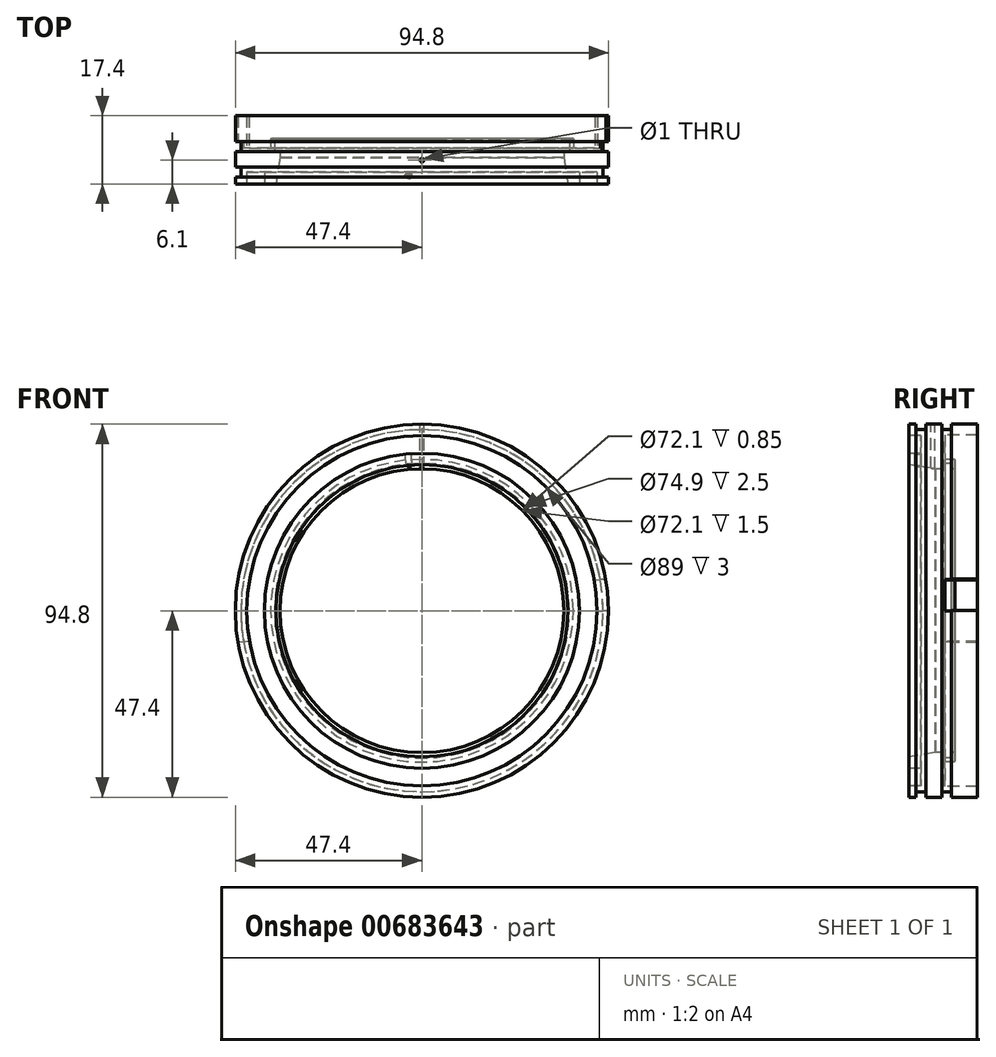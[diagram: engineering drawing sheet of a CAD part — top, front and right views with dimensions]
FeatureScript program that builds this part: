
annotation { "Feature Type Name" : "Feature", "Feature Type Description" : "" }
export const myFeature = defineFeature(function(context is Context, id is Id, definition is map)
    precondition{}
    {
        {
            var Q0;
            Q0=qCreatedBy(makeId("Right.planeOp"),FACE);
            var sketch = newSketch(context, id + "F0", { "sketchPlane" : qUnion([Q0])});
            skLineSegment(sketch, "E0", {"start": v(-21.1, 0) * mm, "end": v(20.57, 0) * mm, "construction": true});
            skLineSegment(sketch, "E1", {"start": v(0, -47.4) * mm, "end": v(1.8, -47.4) * mm});
            skLineSegment(sketch, "E2", {"start": v(1.8, -47.4) * mm, "end": v(1.8, -46) * mm});
            skLineSegment(sketch, "E3", {"start": v(1.8, -46) * mm, "end": v(4.3, -46) * mm});
            skLineSegment(sketch, "E4", {"start": v(4.3, -46) * mm, "end": v(4.3, -47.4) * mm});
            skLineSegment(sketch, "E5", {"start": v(4.3, -47.4) * mm, "end": v(8.3, -47.4) * mm});
            skLineSegment(sketch, "E6", {"start": v(8.3, -47.4) * mm, "end": v(8.3, -46) * mm});
            skLineSegment(sketch, "E7", {"start": v(8.3, -46) * mm, "end": v(10.8, -46) * mm});
            skLineSegment(sketch, "E8", {"start": v(10.8, -46) * mm, "end": v(10.8, -47.4) * mm});
            skLineSegment(sketch, "E9", {"start": v(10.8, -47.4) * mm, "end": v(17.4, -47.4) * mm});
            skLineSegment(sketch, "E10", {"start": v(17.4, -47.4) * mm, "end": v(17.4, -44.6) * mm});
            skLineSegment(sketch, "E11", {"start": v(17.4, -44.6) * mm, "end": v(9.1, -44.6) * mm});
            skLineSegment(sketch, "E12", {"start": v(9.1, -44.6) * mm, "end": v(9.1, -38.45) * mm});
            skLineSegment(sketch, "E13", {"start": v(9.1, -38.45) * mm, "end": v(11.6, -38.45) * mm});
            skLineSegment(sketch, "E14", {"start": v(11.6, -38.45) * mm, "end": v(11.6, -36.05) * mm});
            skLineSegment(sketch, "E15", {"start": v(11.6, -36.05) * mm, "end": v(10.75, -36.05) * mm});
            skLineSegment(sketch, "E16", {"start": v(10.75, -36.05) * mm, "end": v(10.75, -37.45) * mm});
            skLineSegment(sketch, "E17", {"start": v(10.75, -37.45) * mm, "end": v(8.25, -37.45) * mm});
            skLineSegment(sketch, "E18", {"start": v(8.25, -37.45) * mm, "end": v(8.25, -36.05) * mm});
            skLineSegment(sketch, "E19", {"start": v(8.25, -36.05) * mm, "end": v(6.75, -36.05) * mm});
            skLineSegment(sketch, "E20", {"start": v(6.75, -36.05) * mm, "end": v(0, -37.1) * mm});
            skLineSegment(sketch, "E21", {"start": v(0, -37.1) * mm, "end": v(0, -40) * mm});
            skLineSegment(sketch, "E22", {"start": v(0, -40) * mm, "end": v(3, -40) * mm});
            skLineSegment(sketch, "E23", {"start": v(3, -40) * mm, "end": v(3, -44.5) * mm});
            skLineSegment(sketch, "E24", {"start": v(3, -44.5) * mm, "end": v(0, -44.5) * mm});
            skLineSegment(sketch, "E25", {"start": v(0, -44.5) * mm, "end": v(0, -47.4) * mm});
            skSolve(sketch);
        }
        {
            var Q0;
            Q0=makeQuery(id+"F0.imprint","IMPRINT",FACE,{"disambiguationData":[TD([[makeQuery(id+"F0.imprint","IMPRINT",EDGE,{"derivedFrom":sQuery(id+"F0.wireOp",EDGE,"E1")}),1.0]])]});
            var Q1;
            Q1=sQuery(id+"F0.wireOp",EDGE,"E0");
            revolve(context, id + "F1", {"entities" : qUnion([Q0]), "axis" : qUnion([Q1]), "revolveType" : RevolveType.FULL});
        }
        {
            var Q0;
            Q0=qCreatedBy(makeId("Right.planeOp"),FACE);
            cPlane(context, id + "F2", {"entities" : qUnion([Q0]), "cplaneType" : CPlaneType.OFFSET, "offset" : 50 * mm, "width" : 150 * mm, "height" : 150 * mm});
        }
        {
            var Q0;
            Q0=qCreatedBy(id+"F2.planeOp",FACE);
            var sketch = newSketch(context, id + "F3", { "sketchPlane" : qUnion([Q0])});
            skLineSegment(sketch, "E26.bottom", {"start": v(17.4, 4) * mm, "end": v(9.1, 4) * mm});
            skLineSegment(sketch, "E26.top", {"start": v(17.4, -4) * mm, "end": v(9.1, -4) * mm});
            skLineSegment(sketch, "E26.left", {"start": v(17.4, 4) * mm, "end": v(17.4, -4) * mm});
            skLineSegment(sketch, "E26.right", {"start": v(9.1, 4) * mm, "end": v(9.1, -4) * mm});
            skPoint(sketch, "E26.middle", {"position": v(13.25, 0) * mm});
            skSolve(sketch);
        }
        {
            var Q0;
            Q0=makeQuery(id+"F3.imprint","IMPRINT",FACE,{"disambiguationData":[TD([[makeQuery(id+"F3.imprint","IMPRINT",EDGE,{"derivedFrom":sQuery(id+"F3.wireOp",EDGE,"E26.bottom")}),1.0]])]});
            extrude(context, id + "F4", {"entities" : qUnion([Q0]), "operationType" : NewBodyOperationType.REMOVE, "oppositeDirection" : true, "depth" : 10 * mm});
        }
        {
            var Q0;
            Q0=qCreatedBy(makeId("Right.planeOp"),FACE);
            cPlane(context, id + "F5", {"entities" : qUnion([Q0]), "cplaneType" : CPlaneType.OFFSET, "offset" : 50 * mm, "oppositeDirection" : true, "width" : 150 * mm, "height" : 150 * mm});
        }
        {
            var Q0;
            Q0=qCreatedBy(id+"F5.planeOp",FACE);
            var sketch = newSketch(context, id + "F6", { "sketchPlane" : qUnion([Q0])});
            skLineSegment(sketch, "E27.bottom", {"start": v(9.1, -4) * mm, "end": v(17.4, -4) * mm});
            skLineSegment(sketch, "E27.top", {"start": v(9.1, 4) * mm, "end": v(17.4, 4) * mm});
            skLineSegment(sketch, "E27.left", {"start": v(9.1, -4) * mm, "end": v(9.1, 4) * mm});
            skLineSegment(sketch, "E27.right", {"start": v(17.4, -4) * mm, "end": v(17.4, 4) * mm});
            skPoint(sketch, "E27.middle", {"position": v(13.25, 0) * mm});
            skSolve(sketch);
        }
        {
            var Q0;
            Q0=makeQuery(id+"F6.imprint","IMPRINT",FACE,{"disambiguationData":[TD([[makeQuery(id+"F6.imprint","IMPRINT",EDGE,{"derivedFrom":sQuery(id+"F6.wireOp",EDGE,"E27.bottom")}),1.0]])]});
            extrude(context, id + "F7", {"entities" : qUnion([Q0]), "operationType" : NewBodyOperationType.REMOVE, "depth" : 10 * mm});
        }
        {
            var Q0;
            Q0=qCreatedBy(makeId("Top.planeOp"),FACE);
            cPlane(context, id + "F8", {"entities" : qUnion([Q0]), "cplaneType" : CPlaneType.OFFSET, "offset" : 41 * mm, "width" : 150 * mm, "height" : 150 * mm});
        }
        {
            var Q0;
            Q0=qCreatedBy(id+"F8.planeOp",FACE);
            var sketch = newSketch(context, id + "F9", { "sketchPlane" : qUnion([Q0])});
            skPoint(sketch, "E28", {"position": v(0, 2.2) * mm});
            skSolve(sketch);
        }
        {
            var Q0;
            Q0=sQuery(id+"F9.wireOp",VERTEX,"E28");
            var Q1;
            Q1=makeQuery(id+"F1.opRevolve","SWEPT_BODY",BODY,{"disambiguationData":[OSD([sQuery(id+"F0.wireOp",EDGE,"E1"),sQuery(id+"F0.wireOp",EDGE,"E2"),sQuery(id+"F0.wireOp",EDGE,"E3"),sQuery(id+"F0.wireOp",EDGE,"E4"),sQuery(id+"F0.wireOp",EDGE,"E5"),sQuery(id+"F0.wireOp",EDGE,"E6"),sQuery(id+"F0.wireOp",EDGE,"E7"),sQuery(id+"F0.wireOp",EDGE,"E8"),sQuery(id+"F0.wireOp",EDGE,"E9"),sQuery(id+"F0.wireOp",EDGE,"E10"),sQuery(id+"F0.wireOp",EDGE,"E11"),sQuery(id+"F0.wireOp",EDGE,"E12"),sQuery(id+"F0.wireOp",EDGE,"E13"),sQuery(id+"F0.wireOp",EDGE,"E14"),sQuery(id+"F0.wireOp",EDGE,"E15"),sQuery(id+"F0.wireOp",EDGE,"E16"),sQuery(id+"F0.wireOp",EDGE,"E17"),sQuery(id+"F0.wireOp",EDGE,"E18"),sQuery(id+"F0.wireOp",EDGE,"E19"),sQuery(id+"F0.wireOp",EDGE,"E20"),sQuery(id+"F0.wireOp",EDGE,"E21"),sQuery(id+"F0.wireOp",EDGE,"E22"),sQuery(id+"F0.wireOp",EDGE,"E23"),sQuery(id+"F0.wireOp",EDGE,"E24"),sQuery(id+"F0.wireOp",EDGE,"E25")])]});
            hole(context, id + "F10", {"style" : HoleStyle.SIMPLE, "endStyle" : HoleEndStyle.BLIND, "holeDiameter" : 1.5 * mm, "majorDiameter" : 5 * mm, "holeDepth" : 4 * mm, "tappedDepth" : 12 * mm, "tapClearance" : 3, "startFromSketch" : true, "locations" : qUnion([Q0]), "scope" : qUnion([Q1])});
        }
        {
            var Q0;
            Q0=qCreatedBy(makeId("Top.planeOp"),FACE);
            cPlane(context, id + "F11", {"entities" : qUnion([Q0]), "cplaneType" : CPlaneType.OFFSET, "offset" : 48 * mm, "width" : 150 * mm, "height" : 150 * mm});
        }
        {
            var Q0;
            Q0=qCreatedBy(id+"F11.planeOp",FACE);
            var sketch = newSketch(context, id + "F12", { "sketchPlane" : qUnion([Q0])});
            skPoint(sketch, "E29", {"position": v(0, 6.1) * mm});
            skSolve(sketch);
        }
        {
            var Q0;
            Q0=makeQuery(id+"F1.opRevolve","SWEPT_BODY",BODY,{"disambiguationData":[OSD([sQuery(id+"F0.wireOp",EDGE,"E1"),sQuery(id+"F0.wireOp",EDGE,"E2"),sQuery(id+"F0.wireOp",EDGE,"E3"),sQuery(id+"F0.wireOp",EDGE,"E4"),sQuery(id+"F0.wireOp",EDGE,"E5"),sQuery(id+"F0.wireOp",EDGE,"E6"),sQuery(id+"F0.wireOp",EDGE,"E7"),sQuery(id+"F0.wireOp",EDGE,"E8"),sQuery(id+"F0.wireOp",EDGE,"E9"),sQuery(id+"F0.wireOp",EDGE,"E10"),sQuery(id+"F0.wireOp",EDGE,"E11"),sQuery(id+"F0.wireOp",EDGE,"E12"),sQuery(id+"F0.wireOp",EDGE,"E13"),sQuery(id+"F0.wireOp",EDGE,"E14"),sQuery(id+"F0.wireOp",EDGE,"E15"),sQuery(id+"F0.wireOp",EDGE,"E16"),sQuery(id+"F0.wireOp",EDGE,"E17"),sQuery(id+"F0.wireOp",EDGE,"E18"),sQuery(id+"F0.wireOp",EDGE,"E19"),sQuery(id+"F0.wireOp",EDGE,"E20"),sQuery(id+"F0.wireOp",EDGE,"E21"),sQuery(id+"F0.wireOp",EDGE,"E22"),sQuery(id+"F0.wireOp",EDGE,"E23"),sQuery(id+"F0.wireOp",EDGE,"E24"),sQuery(id+"F0.wireOp",EDGE,"E25")])]});
            var Q1;
            Q1=makeQuery(id+"F1.opRevolve","SWEPT_EDGE",EDGE,{"disambiguationData":[OSD([sQuery(id+"F0.wireOp",EDGE,"E1"),sQuery(id+"F0.wireOp",EDGE,"E25")])]});
            transform(context, id + "F13", {"entities" : qUnion([Q0]), "transformType" : TransformType.ROTATION, "transformAxis" : qUnion([Q1]), "angle" : 5 * degree, "makeCopy" : false});
        }
        {
            var Q0;
            Q0=sQuery(id+"F12.wireOp",VERTEX,"E29");
            var Q1;
            Q1=makeQuery(id+"F1.opRevolve","SWEPT_BODY",BODY,{"disambiguationData":[OSD([sQuery(id+"F0.wireOp",EDGE,"E1"),sQuery(id+"F0.wireOp",EDGE,"E2"),sQuery(id+"F0.wireOp",EDGE,"E3"),sQuery(id+"F0.wireOp",EDGE,"E4"),sQuery(id+"F0.wireOp",EDGE,"E5"),sQuery(id+"F0.wireOp",EDGE,"E6"),sQuery(id+"F0.wireOp",EDGE,"E7"),sQuery(id+"F0.wireOp",EDGE,"E8"),sQuery(id+"F0.wireOp",EDGE,"E9"),sQuery(id+"F0.wireOp",EDGE,"E10"),sQuery(id+"F0.wireOp",EDGE,"E11"),sQuery(id+"F0.wireOp",EDGE,"E12"),sQuery(id+"F0.wireOp",EDGE,"E13"),sQuery(id+"F0.wireOp",EDGE,"E14"),sQuery(id+"F0.wireOp",EDGE,"E15"),sQuery(id+"F0.wireOp",EDGE,"E16"),sQuery(id+"F0.wireOp",EDGE,"E17"),sQuery(id+"F0.wireOp",EDGE,"E18"),sQuery(id+"F0.wireOp",EDGE,"E19"),sQuery(id+"F0.wireOp",EDGE,"E20"),sQuery(id+"F0.wireOp",EDGE,"E21"),sQuery(id+"F0.wireOp",EDGE,"E22"),sQuery(id+"F0.wireOp",EDGE,"E23"),sQuery(id+"F0.wireOp",EDGE,"E24"),sQuery(id+"F0.wireOp",EDGE,"E25")])]});
            hole(context, id + "F14", {"style" : HoleStyle.SIMPLE, "endStyle" : HoleEndStyle.BLIND, "holeDiameter" : 1 * mm, "majorDiameter" : 5 * mm, "holeDepth" : 20 * mm, "tappedDepth" : 12 * mm, "tapClearance" : 3, "startFromSketch" : true, "locations" : qUnion([Q0]), "scope" : qUnion([Q1])});
        }
    });
